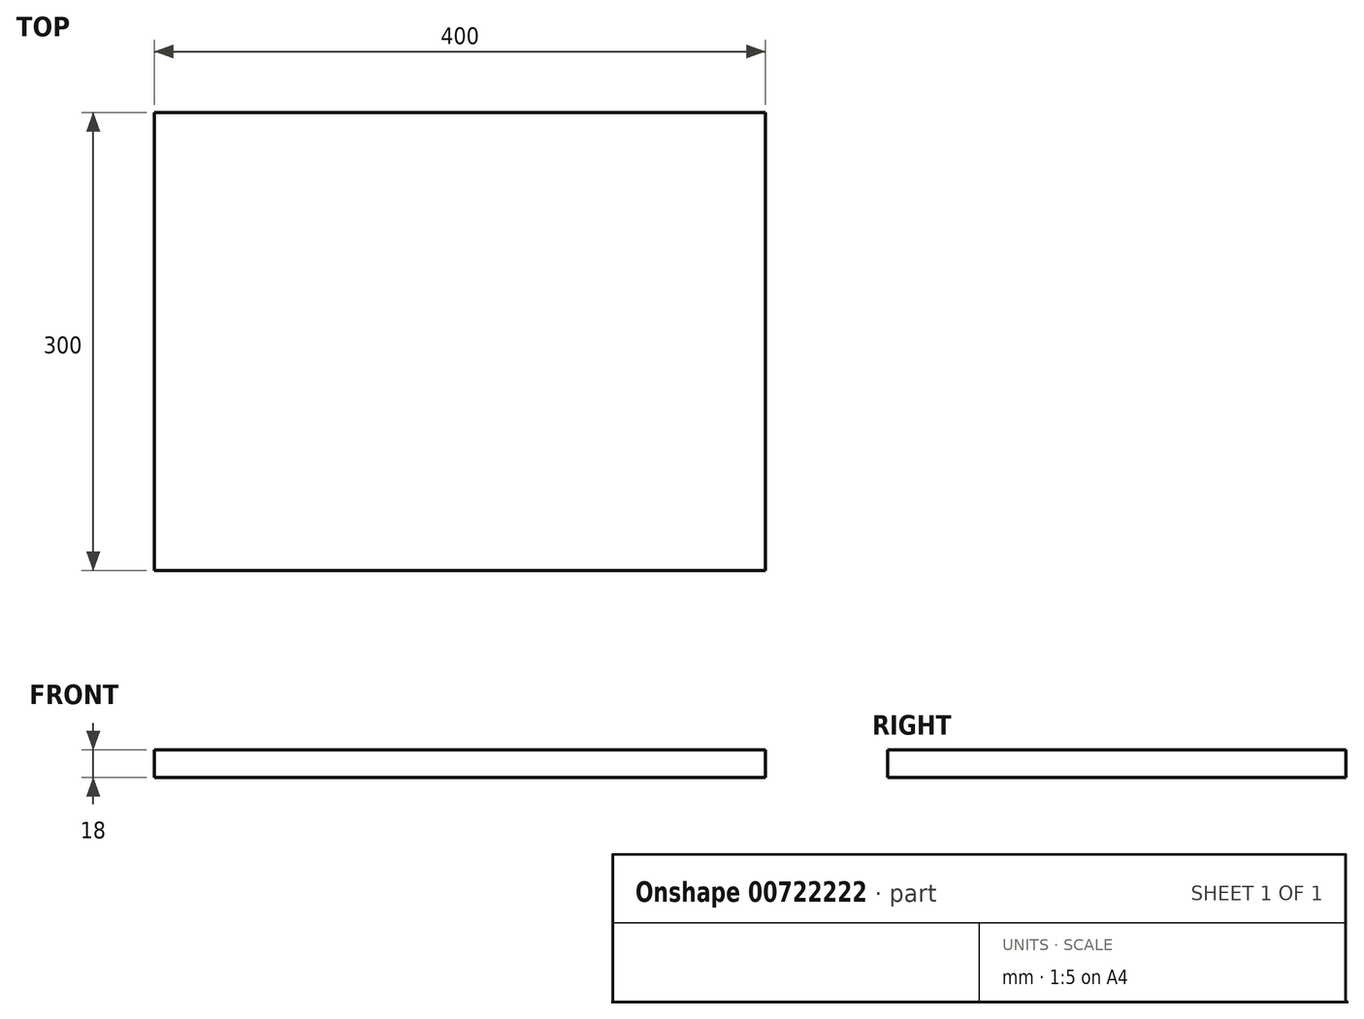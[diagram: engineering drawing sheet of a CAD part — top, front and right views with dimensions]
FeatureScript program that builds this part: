
annotation { "Feature Type Name" : "Feature", "Feature Type Description" : "" }
export const myFeature = defineFeature(function(context is Context, id is Id, definition is map)
    precondition{}
    {
        {
            var Q0;
            Q0=qCreatedBy(makeId("Top.planeOp"),FACE);
            var sketch = newSketch(context, id + "F0", { "sketchPlane" : qUnion([Q0])});
            skLineSegment(sketch, "E0.bottom", {"start": v(-200, 150) * mm, "end": v(200, 150) * mm});
            skLineSegment(sketch, "E0.top", {"start": v(-200, -150) * mm, "end": v(200, -150) * mm});
            skLineSegment(sketch, "E0.left", {"start": v(-200, 150) * mm, "end": v(-200, -150) * mm});
            skLineSegment(sketch, "E0.right", {"start": v(200, 150) * mm, "end": v(200, -150) * mm});
            skSolve(sketch);
        }
        {
            var Q0;
            Q0=makeQuery(id+"F0.imprint","IMPRINT",FACE,{"disambiguationData":[TD([[makeQuery(id+"F0.imprint","IMPRINT",EDGE,{"derivedFrom":sQuery(id+"F0.wireOp",EDGE,"E0.bottom")}),-1.0]])]});
            extrude(context, id + "F1", {"entities" : qUnion([Q0]), "depth" : 18 * mm, "offsetDistance" : 25 * mm});
        }
    });
